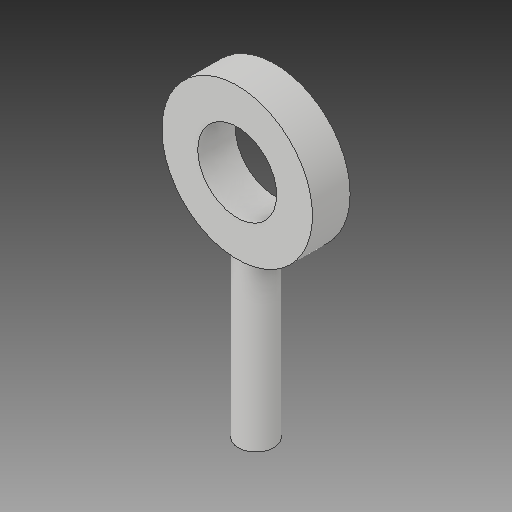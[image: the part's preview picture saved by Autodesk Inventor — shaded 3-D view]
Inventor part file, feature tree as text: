
AUTODESK INVENTOR PART (.ipt)
format: ipt  version: 2018 (Build 220112000, 112)  size: 99,328 bytes
history: native  units: in
note: dims shown in document units (in); Inventor stores cm internally (conversion verified against a paired STEP export)
features: other x3, sketch x2, plane x2
ambient origin geometry x8: Origin, YZ Plane, XZ Plane, XY Plane, X Axis, Y Axis, Z Axis, Center Point
bodies: Solid1 (feature_tree)
feature tree (7):
  other  "eye screw stand-in.ipt"
  other  "Solid1::eye screw stand-in.ipt"
  other  "TaggingFeature1"
  sketch  "Sketch2"  dims[d0=0.3937in]
  sketch  "Sketch3"
  plane  "Work Plane1"
  plane  "Work Plane2"
